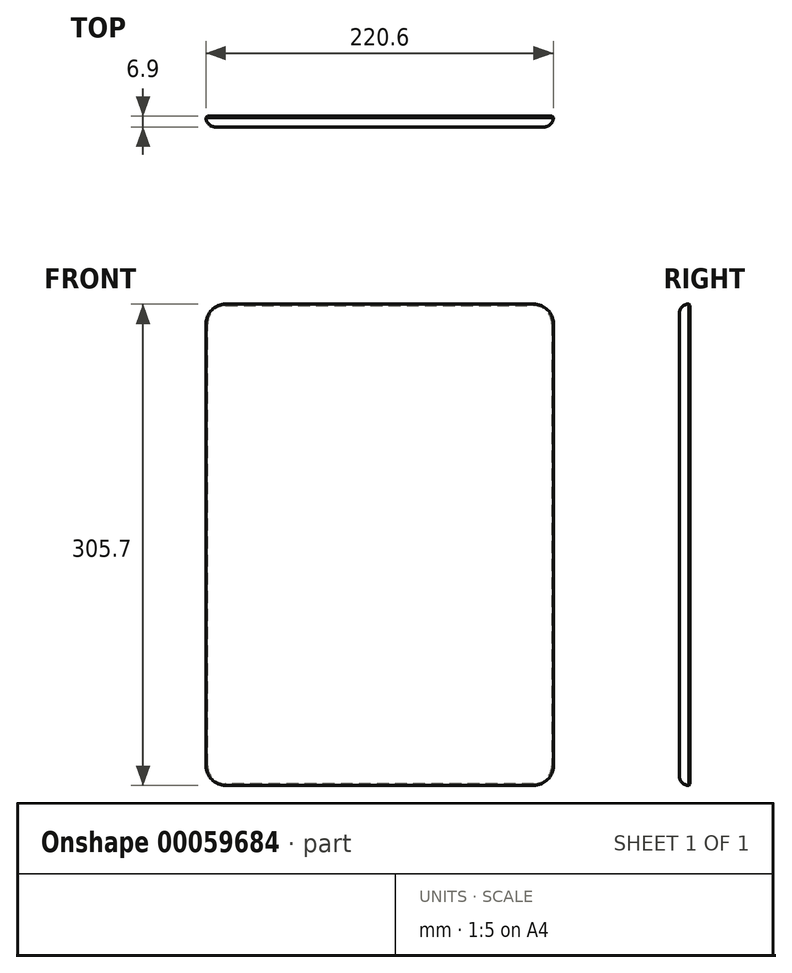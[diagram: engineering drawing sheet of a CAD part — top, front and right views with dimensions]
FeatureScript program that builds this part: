
annotation { "Feature Type Name" : "Feature", "Feature Type Description" : "" }
export const myFeature = defineFeature(function(context is Context, id is Id, definition is map)
    precondition{}
    {
        {
            var Q0;
            Q0=qCreatedBy(makeId("Front.planeOp"),FACE);
            var sketch = newSketch(context, id + "F0", { "sketchPlane" : qUnion([Q0])});
            skLineSegment(sketch, "E0.rect.bottom", {"start": v(110.3, 152.85) * mm, "end": v(-110.3, 152.85) * mm, "construction": true});
            skLineSegment(sketch, "E0.rect.top", {"start": v(110.3, -152.85) * mm, "end": v(-110.3, -152.85) * mm, "construction": true});
            skLineSegment(sketch, "E0.rect.left", {"start": v(110.3, 152.85) * mm, "end": v(110.3, -152.85) * mm, "construction": true});
            skLineSegment(sketch, "E0.rect.right", {"start": v(-110.3, 152.85) * mm, "end": v(-110.3, -152.85) * mm, "construction": true});
            skPoint(sketch, "E0.rect.middle", {"position": v(0, 0) * mm});
            skArc(sketch, "E1", {"start": v(-97.8, 152.85) * mm, "mid": v(-106.64, 149.19) * mm, "end": v(-110.3, 140.35) * mm});
            skArc(sketch, "E2", {"start": v(110.3, 140.35) * mm, "mid": v(106.64, 149.19) * mm, "end": v(97.8, 152.85) * mm});
            skArc(sketch, "E3", {"start": v(97.8, -152.85) * mm, "mid": v(106.64, -149.19) * mm, "end": v(110.3, -140.35) * mm});
            skArc(sketch, "E4", {"start": v(-110.3, -140.35) * mm, "mid": v(-106.64, -149.19) * mm, "end": v(-97.8, -152.85) * mm});
            skLineSegment(sketch, "E5", {"start": v(-97.8, 152.85) * mm, "end": v(97.8, 152.85) * mm});
            skLineSegment(sketch, "E6", {"start": v(110.3, 140.35) * mm, "end": v(110.3, -140.35) * mm});
            skLineSegment(sketch, "E7", {"start": v(97.8, -152.85) * mm, "end": v(-97.8, -152.85) * mm});
            skLineSegment(sketch, "E8", {"start": v(-110.3, -140.35) * mm, "end": v(-110.3, 140.35) * mm});
            skSolve(sketch);
        }
        {
            var Q0;
            Q0=makeQuery(id+"F0.imprint","IMPRINT",FACE,{"disambiguationData":[TD([[makeQuery(id+"F0.imprint","IMPRINT",EDGE,{"derivedFrom":sQuery(id+"F0.wireOp",EDGE,"E1")}),1.0]])]});
            extrude(context, id + "F1", {"entities" : qUnion([Q0]), "depth" : 6.9 * mm});
        }
        {
            var Q0;
            Q0=makeQuery(id+"F1.opExtrude","CAP_FACE",FACE,{"disambiguationData":[OSD([sQuery(id+"F0.wireOp",EDGE,"E1"),sQuery(id+"F0.wireOp",EDGE,"E2"),sQuery(id+"F0.wireOp",EDGE,"E3"),sQuery(id+"F0.wireOp",EDGE,"E4"),sQuery(id+"F0.wireOp",EDGE,"E5"),sQuery(id+"F0.wireOp",EDGE,"E6"),sQuery(id+"F0.wireOp",EDGE,"E7"),sQuery(id+"F0.wireOp",EDGE,"E8")])],"isStart":false});
            fillet(context, id + "F2", {"entities" : qUnion([Q0]), "radius" : 6 * mm, "tangentPropagation" : true, "allowEdgeOverflow" : false});
        }
        {
            var Q0;
            Q0=makeQuery(id+"F1.opExtrude","CAP_FACE",FACE,{"disambiguationData":[OSD([sQuery(id+"F0.wireOp",EDGE,"E1"),sQuery(id+"F0.wireOp",EDGE,"E2"),sQuery(id+"F0.wireOp",EDGE,"E3"),sQuery(id+"F0.wireOp",EDGE,"E4"),sQuery(id+"F0.wireOp",EDGE,"E5"),sQuery(id+"F0.wireOp",EDGE,"E6"),sQuery(id+"F0.wireOp",EDGE,"E7"),sQuery(id+"F0.wireOp",EDGE,"E8")])],"isStart":true});
            chamfer(context, id + "F3", {"entities" : qUnion([Q0]), "width" : .9 * mm, "tangentPropagation" : true});
        }
    });
